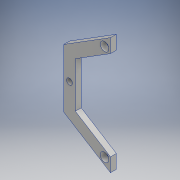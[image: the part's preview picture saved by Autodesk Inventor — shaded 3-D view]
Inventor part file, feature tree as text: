
AUTODESK INVENTOR PART (.ipt)
format: ipt  version: 2018.1 (Build 221171000, 171)  size: 123,904 bytes
history: native  units: mm
features: extrude x2, sketch x2, other x1
ambient origin geometry x8: Origin, YZ Plane, XZ Plane, XY Plane, X Axis, Y Axis, Z Axis, Center Point
bodies: Body1 (feature_tree)
feature tree (5):
  other  "ソリッド1"
  extrude  "押し出し1"  Depth=10.0mm
  extrude  "押し出し2"  Depth=25.0mm
  sketch  "スケッチ1"
  sketch  "スケッチ2"
